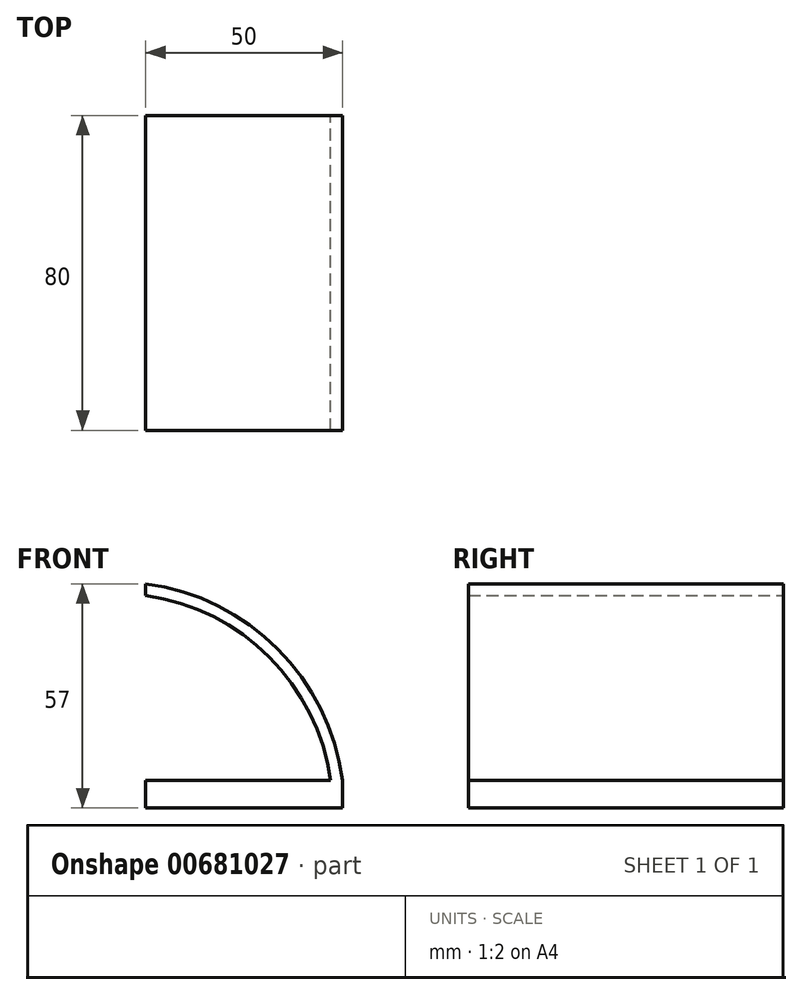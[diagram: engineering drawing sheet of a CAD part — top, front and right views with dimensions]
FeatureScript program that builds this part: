
annotation { "Feature Type Name" : "Feature", "Feature Type Description" : "" }
export const myFeature = defineFeature(function(context is Context, id is Id, definition is map)
    precondition{}
    {
        {
            var Q0;
            Q0=qCreatedBy(makeId("Front.planeOp"),FACE);
            var sketch = newSketch(context, id + "F0", { "sketchPlane" : qUnion([Q0])});
            skArc(sketch, "E0", {"start": v(47, 5.44) * mm, "mid": v(31.38, 36.82) * mm, "end": v(0, 52.44) * mm});
            skArc(sketch, "E1", {"start": v(50, 5.44) * mm, "mid": v(33.48, 38.92) * mm, "end": v(0, 55.44) * mm});
            skLineSegment(sketch, "E2", {"start": v(0, 55.44) * mm, "end": v(0, 52.44) * mm});
            skLineSegment(sketch, "E3", {"start": v(50, 5.44) * mm, "end": v(68.95, 5.44) * mm});
            skLineSegment(sketch, "E4.bottom", {"start": v(50, 5.44) * mm, "end": v(0, 5.44) * mm});
            skLineSegment(sketch, "E4.top", {"start": v(50, -1.56) * mm, "end": v(0, -1.56) * mm});
            skLineSegment(sketch, "E4.left", {"start": v(50, 5.44) * mm, "end": v(50, -1.56) * mm});
            skLineSegment(sketch, "E4.right", {"start": v(0, 5.44) * mm, "end": v(0, -1.56) * mm});
            skPoint(sketch, "E4.middle", {"position": v(25, 1.94) * mm});
            skSolve(sketch);
        }
        {
            var Q0;
            {var subQ3=sQuery(id+"F0.wireOp",EDGE,"E0");Q0=makeQuery(id+"F0.imprint","IMPRINT",FACE,{"disambiguationData":[TD([[makeQuery(id+"F0.imprint","IMPRINT",EDGE,{"derivedFrom":subQ3}),-1.0]])]});}
            var Q1;
            Q1=makeQuery(id+"F0.imprint","IMPRINT",FACE,{"disambiguationData":[TD([[makeQuery(id+"F0.imprint","IMPRINT",EDGE,{"derivedFrom":sQuery(id+"F0.wireOp",EDGE,"E4.top")}),-1.0]])]});
            extrude(context, id + "F1", {"entities" : qUnion([Q0, Q1]), "depth" : 80 * mm, "offsetDistance" : 25.4 * mm});
        }
    });
